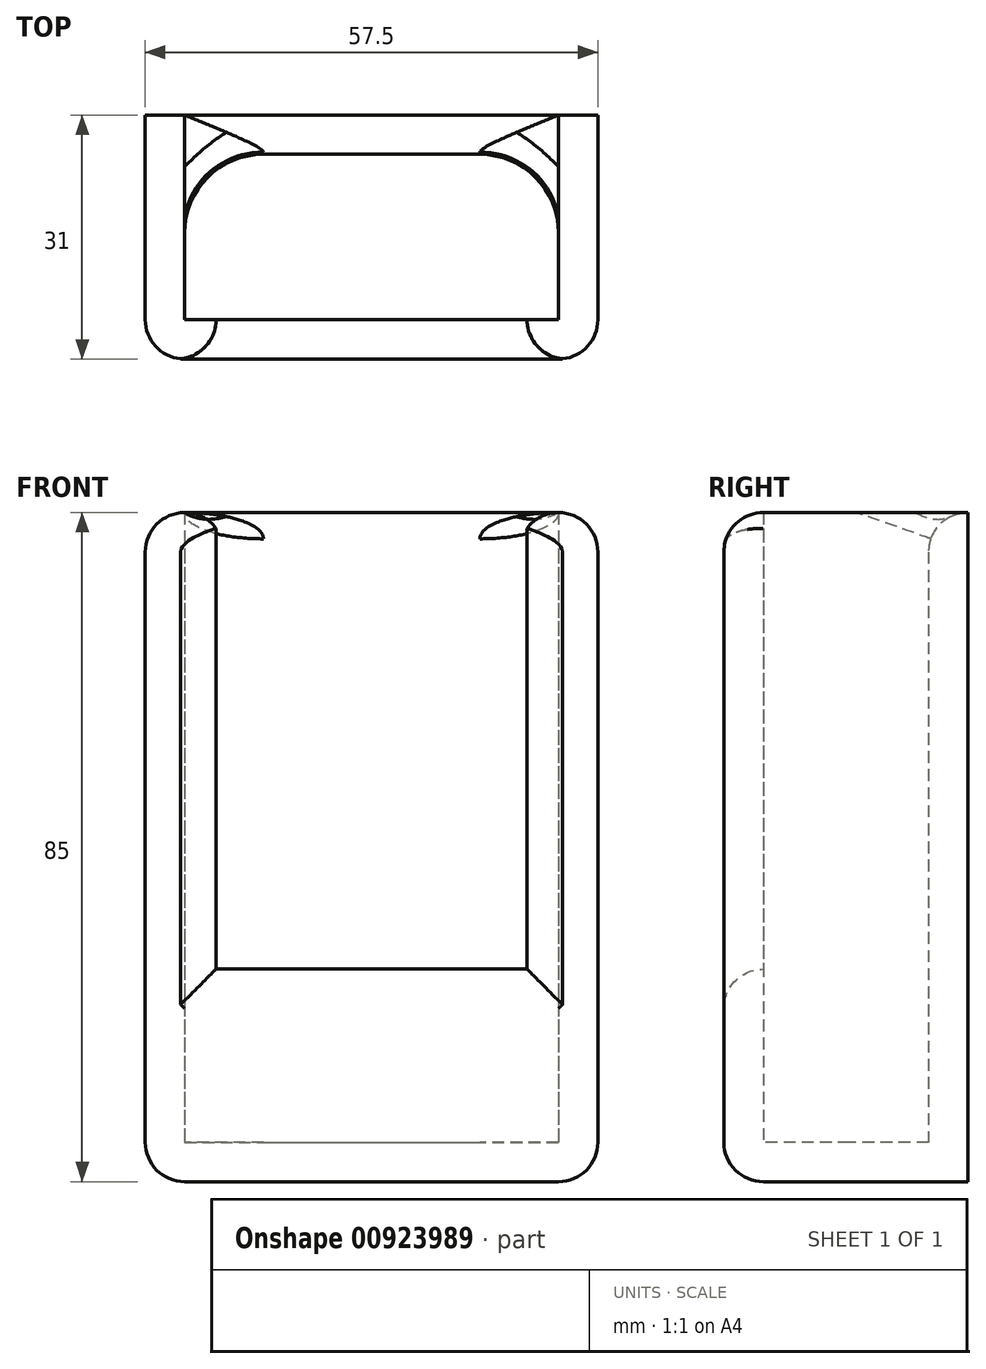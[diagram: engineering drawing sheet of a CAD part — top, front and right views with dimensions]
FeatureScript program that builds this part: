
annotation { "Feature Type Name" : "Feature", "Feature Type Description" : "" }
export const myFeature = defineFeature(function(context is Context, id is Id, definition is map)
    precondition{}
    {
        {
            var Q0;
            Q0=qCreatedBy(makeId("Top.planeOp"),FACE);
            var sketch = newSketch(context, id + "F0", { "sketchPlane" : qUnion([Q0])});
            skLineSegment(sketch, "E0.bottom", {"start": v(-23.75, 14.1) * mm, "end": v(23.75, 14.1) * mm});
            skLineSegment(sketch, "E0.top", {"start": v(-23.75, -6.9) * mm, "end": v(23.75, -6.9) * mm});
            skLineSegment(sketch, "E0.left", {"start": v(-23.75, 14.1) * mm, "end": v(-23.75, -6.9) * mm});
            skLineSegment(sketch, "E0.right", {"start": v(23.75, 14.1) * mm, "end": v(23.75, -6.9) * mm});
            skLineSegment(sketch, "E1.bottom", {"start": v(-28.75, 19.1) * mm, "end": v(28.75, 19.1) * mm});
            skLineSegment(sketch, "E1.top", {"start": v(-28.75, -11.9) * mm, "end": v(28.75, -11.9) * mm});
            skLineSegment(sketch, "E1.left", {"start": v(-28.75, 19.1) * mm, "end": v(-28.75, -11.9) * mm});
            skLineSegment(sketch, "E1.right", {"start": v(28.75, 19.1) * mm, "end": v(28.75, -11.9) * mm});
            skSolve(sketch);
        }
        {
            var Q0;
            Q0 = qSketchRegion(id + "F0", true);
            extrude(context, id + "F1", {"entities" : qUnion([Q0]), "depth" : 80 * mm, "offsetDistance" : 25 * mm});
        }
        {
            var Q0;
            Q0=makeQuery(id+"F0.imprint","IMPRINT",FACE,{"disambiguationData":[TD([[makeQuery(id+"F0.imprint","IMPRINT",EDGE,{"derivedFrom":sQuery(id+"F0.wireOp",EDGE,"E0.bottom")}),1.0]])]});
            var Q1;
            Q1=makeQuery(id+"F0.imprint","IMPRINT",FACE,{"disambiguationData":[TD([[makeQuery(id+"F0.imprint","IMPRINT",EDGE,{"derivedFrom":sQuery(id+"F0.wireOp",EDGE,"E0.bottom")}),-1.0]])]});
            extrude(context, id + "F2", {"entities" : qUnion([Q0, Q1]), "operationType" : NewBodyOperationType.ADD, "oppositeDirection" : true, "depth" : 5 * mm, "offsetDistance" : 25 * mm});
        }
        {
            var Q0;
            Q0=makeQuery(id+"F1.opExtrude","SWEPT_FACE",FACE,{"disambiguationData":[OSD([sQuery(id+"F0.wireOp",EDGE,"E0.top")])]});
            var sketch = newSketch(context, id + "F3", { "sketchPlane" : qUnion([Q0])});
            skLineSegment(sketch, "E2.bottom", {"start": v(19.75, 80) * mm, "end": v(-19.75, 80) * mm});
            skLineSegment(sketch, "E2.top", {"start": v(19.75, 22) * mm, "end": v(-19.75, 22) * mm});
            skLineSegment(sketch, "E2.left", {"start": v(19.75, 80) * mm, "end": v(19.75, 22) * mm});
            skLineSegment(sketch, "E2.right", {"start": v(-19.75, 80) * mm, "end": v(-19.75, 22) * mm});
            skSolve(sketch);
        }
        {
            var Q0;
            Q0 = qSketchRegion(id + "F3", true);
            extrude(context, id + "F4", {"entities" : qUnion([Q0]), "operationType" : NewBodyOperationType.REMOVE, "oppositeDirection" : true, "depth" : 25 * mm, "offsetDistance" : 25 * mm});
        }
        {
            var Q0;
            Q0=makeQuery(id+"F2.opExtrude","CAP_EDGE",EDGE,{"disambiguationData":[OSD([sQuery(id+"F0.wireOp",EDGE,"E1.top")])],"isStart":false});
            var Q1;
            {var subQ0=sQuery(id+"F0.wireOp",EDGE,"E1.left");var subQ1=sQuery(id+"F0.wireOp",EDGE,"E1.top");Q1=makeQuery(id+"F2.boolean.opBoolean","MERGE",EDGE,{"derivedFrom":[makeQuery(id+"F1.opExtrude","SWEPT_EDGE",EDGE,{"disambiguationData":[OSD([subQ1,subQ0])]}),makeQuery(id+"F2.opExtrude","SWEPT_EDGE",EDGE,{"disambiguationData":[OSD([subQ1,subQ0])]})]});}
            var Q2;
            {var subQ0=sQuery(id+"F0.wireOp",EDGE,"E1.right");var subQ1=sQuery(id+"F0.wireOp",EDGE,"E1.top");Q2=makeQuery(id+"F2.boolean.opBoolean","MERGE",EDGE,{"derivedFrom":[makeQuery(id+"F1.opExtrude","SWEPT_EDGE",EDGE,{"disambiguationData":[OSD([subQ1,subQ0])]}),makeQuery(id+"F2.opExtrude","SWEPT_EDGE",EDGE,{"disambiguationData":[OSD([subQ1,subQ0])]})]});}
            var Q3;
            {var subQ0=sQuery(id+"F0.wireOp",EDGE,"E1.top");Q3=makeQuery(id+"F4.boolean.opBoolean","INTERSECT",EDGE,{"derivedFrom":[makeQuery(id+"F2.boolean.opBoolean","MERGE",FACE,{"derivedFrom":[makeQuery(id+"F1.opExtrude","SWEPT_FACE",FACE,{"disambiguationData":[OSD([subQ0])]}),makeQuery(id+"F2.opExtrude","SWEPT_FACE",FACE,{"disambiguationData":[OSD([subQ0])]})]}),makeQuery(id+"F4.opExtrude","SWEPT_FACE",FACE,{"disambiguationData":[OSD([sQuery(id+"F3.wireOp",EDGE,"E2.top")])]})]});}
            var Q4;
            {var subQ0=sQuery(id+"F0.wireOp",EDGE,"E1.top");Q4=makeQuery(id+"F4.boolean.opBoolean","INTERSECT",EDGE,{"derivedFrom":[makeQuery(id+"F2.boolean.opBoolean","MERGE",FACE,{"derivedFrom":[makeQuery(id+"F1.opExtrude","SWEPT_FACE",FACE,{"disambiguationData":[OSD([subQ0])]}),makeQuery(id+"F2.opExtrude","SWEPT_FACE",FACE,{"disambiguationData":[OSD([subQ0])]})]}),makeQuery(id+"F4.opExtrude","SWEPT_FACE",FACE,{"disambiguationData":[OSD([sQuery(id+"F3.wireOp",EDGE,"E2.left")])]})]});}
            var Q5;
            {var subQ0=sQuery(id+"F0.wireOp",EDGE,"E1.top");Q5=makeQuery(id+"F4.boolean.opBoolean","INTERSECT",EDGE,{"derivedFrom":[makeQuery(id+"F2.boolean.opBoolean","MERGE",FACE,{"derivedFrom":[makeQuery(id+"F1.opExtrude","SWEPT_FACE",FACE,{"disambiguationData":[OSD([subQ0])]}),makeQuery(id+"F2.opExtrude","SWEPT_FACE",FACE,{"disambiguationData":[OSD([subQ0])]})]}),makeQuery(id+"F4.opExtrude","SWEPT_FACE",FACE,{"disambiguationData":[OSD([sQuery(id+"F3.wireOp",EDGE,"E2.right")])]})]});}
            fillet(context, id + "F5", {"entities" : qUnion([Q0, Q1, Q2, Q3, Q4, Q5]), "radius" : 5 * mm, "tangentPropagation" : true, "allowEdgeOverflow" : false});
        }
        {
            var Q0;
            Q0=makeQuery(id+"F2.opExtrude","CAP_EDGE",EDGE,{"disambiguationData":[OSD([sQuery(id+"F0.wireOp",EDGE,"E1.right")])],"isStart":false});
            var Q1;
            Q1=makeQuery(id+"F2.opExtrude","CAP_EDGE",EDGE,{"disambiguationData":[OSD([sQuery(id+"F0.wireOp",EDGE,"E1.left")])],"isStart":false});
            fillet(context, id + "F6", {"entities" : qUnion([Q0, Q1]), "radius" : 5 * mm, "tangentPropagation" : true, "allowEdgeOverflow" : false});
        }
        {
            var Q0;
            {var subQ0=sQuery(id+"F0.wireOp",EDGE,"E1.right");var subQ1=sQuery(id+"F0.wireOp",EDGE,"E1.top");Q0=makeQuery(id+"F5.opFillet","BLEND_EDGE",EDGE,{"blendedFrom":[makeQuery(id+"F2.boolean.opBoolean","MERGE",EDGE,{"derivedFrom":[makeQuery(id+"F1.opExtrude","SWEPT_EDGE",EDGE,{"disambiguationData":[OSD([subQ1,subQ0])]}),makeQuery(id+"F2.opExtrude","SWEPT_EDGE",EDGE,{"disambiguationData":[OSD([subQ1,subQ0])]})]}),makeQuery(id+"F1.opExtrude","CAP_FACE",FACE,{"disambiguationData":[OSD([sQuery(id+"F0.wireOp",EDGE,"E0.bottom"),sQuery(id+"F0.wireOp",EDGE,"E0.top"),sQuery(id+"F0.wireOp",EDGE,"E0.left"),sQuery(id+"F0.wireOp",EDGE,"E0.right"),sQuery(id+"F0.wireOp",EDGE,"E1.bottom"),subQ1,sQuery(id+"F0.wireOp",EDGE,"E1.left"),subQ0])],"isStart":false})],"blendedInto":[makeQuery(id+"F1.opExtrude","CAP_FACE",FACE,{"disambiguationData":[OSD([sQuery(id+"F0.wireOp",EDGE,"E0.bottom"),sQuery(id+"F0.wireOp",EDGE,"E0.top"),sQuery(id+"F0.wireOp",EDGE,"E0.left"),sQuery(id+"F0.wireOp",EDGE,"E0.right"),sQuery(id+"F0.wireOp",EDGE,"E1.bottom"),subQ1,sQuery(id+"F0.wireOp",EDGE,"E1.left"),subQ0])],"isStart":false})]});}
            var Q1;
            Q1=makeQuery(id+"F1.opExtrude","CAP_EDGE",EDGE,{"disambiguationData":[OSD([sQuery(id+"F0.wireOp",EDGE,"E1.left")])],"isStart":false});
            fillet(context, id + "F7", {"entities" : qUnion([Q0, Q1]), "radius" : 5 * mm, "tangentPropagation" : true, "allowEdgeOverflow" : false});
        }
        {
            var Q0;
            Q0=makeQuery(id+"F1.opExtrude","CAP_EDGE",EDGE,{"disambiguationData":[OSD([sQuery(id+"F0.wireOp",EDGE,"E0.bottom")])],"isStart":false});
            fillet(context, id + "F8", {"entities" : qUnion([Q0]), "radius" : 5 * mm, "tangentPropagation" : true, "allowEdgeOverflow" : false});
        }
        {
            var Q0;
            Q0=makeQuery(id+"F1.opExtrude","SWEPT_EDGE",EDGE,{"disambiguationData":[OSD([sQuery(id+"F0.wireOp",EDGE,"E0.bottom"),sQuery(id+"F0.wireOp",EDGE,"E0.right")])]});
            var Q1;
            Q1=makeQuery(id+"F1.opExtrude","SWEPT_EDGE",EDGE,{"disambiguationData":[OSD([sQuery(id+"F0.wireOp",EDGE,"E0.bottom"),sQuery(id+"F0.wireOp",EDGE,"E0.left")])]});
            fillet(context, id + "F9", {"entities" : qUnion([Q0, Q1]), "radius" : 10 * mm, "tangentPropagation" : true, "allowEdgeOverflow" : false});
        }
    });
